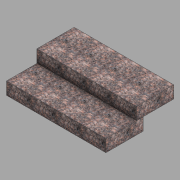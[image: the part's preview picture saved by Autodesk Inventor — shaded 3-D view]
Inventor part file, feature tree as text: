
AUTODESK INVENTOR PART (.ipt)
format: ipt  version: 2022.2 (Build 262287000, 287)  size: 134,144 bytes
history: native  units: in
note: dims shown in document units (in); Inventor stores cm internally (conversion verified against a paired STEP export)
features: extrude x2, sketch x2
ambient origin geometry x8: Origin, YZ Plane, XZ Plane, XY Plane, X Axis, Y Axis, Z Axis, Center Point
bodies: Solid1 (feature_tree)
feature tree (4):
  extrude  "Extrusion1"  Depth=18.0in
  sketch  "Sketch1"  dims[d0=48.0in d1=18.0in]
  sketch  "Sketch2"  dims[d2=6.0in d3=0.0in d4=48.0625in d5=18.0in d7=0.0in d8=6.0in]
  extrude  "Extrusion2"  Depth=48.0625in TaperAngle=0.0deg
